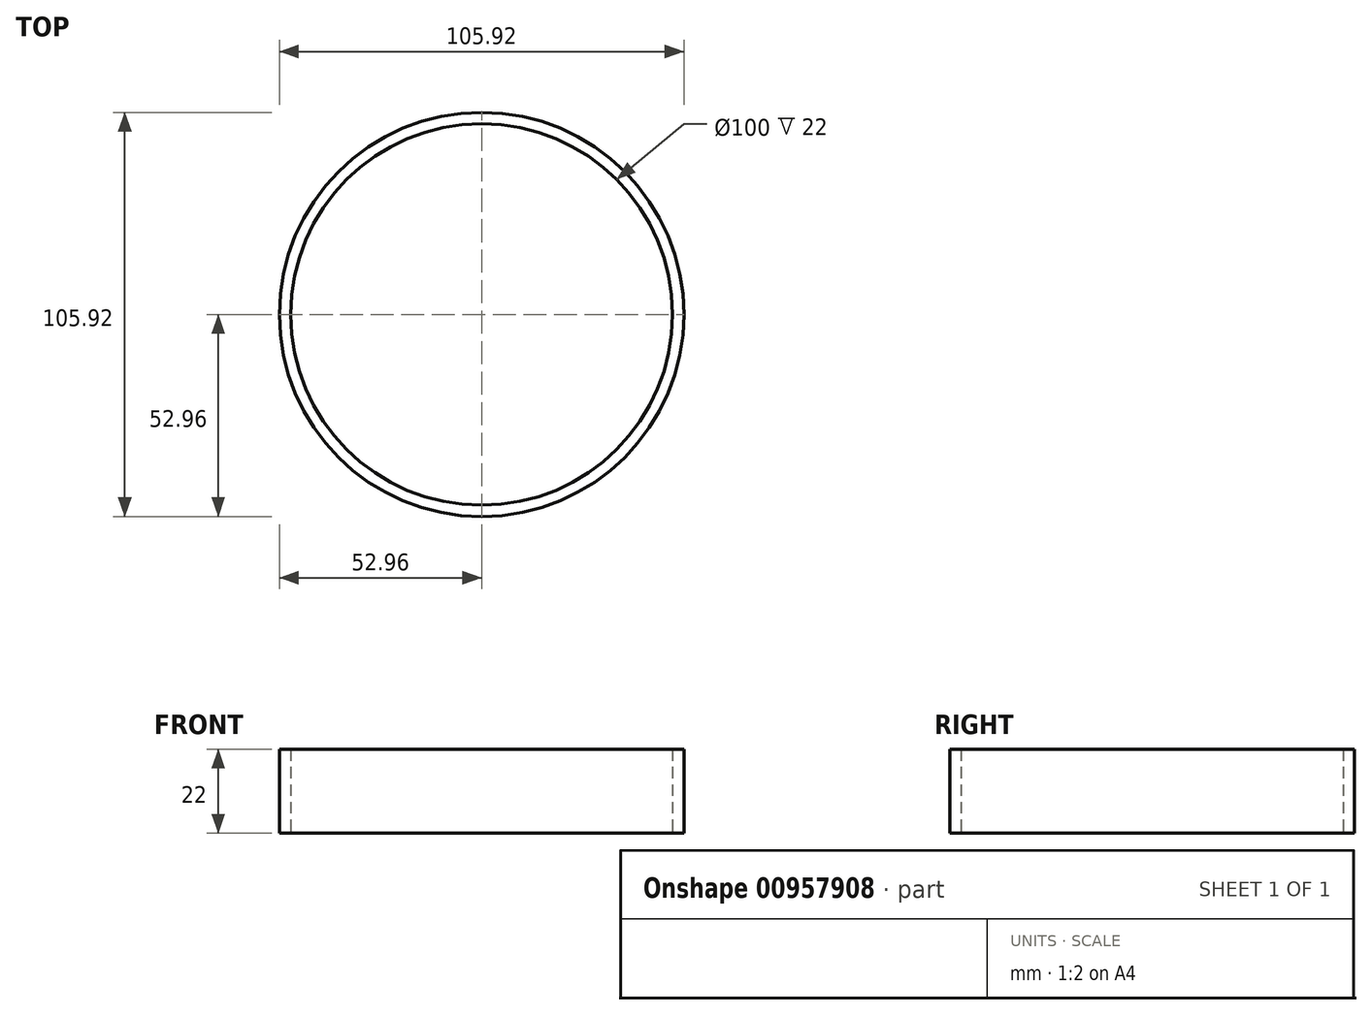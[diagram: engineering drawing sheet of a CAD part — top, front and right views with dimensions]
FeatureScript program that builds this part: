
annotation { "Feature Type Name" : "Feature", "Feature Type Description" : "" }
export const myFeature = defineFeature(function(context is Context, id is Id, definition is map)
    precondition{}
    {
        {
            var Q0;
            Q0=qCreatedBy(makeId("Top.planeOp"),FACE);
            var sketch = newSketch(context, id + "F0", { "sketchPlane" : qUnion([Q0])});
            skCircle(sketch, "E0", {"center": v(0, 0) * mm, "radius": 50 * mm});
            skCircle(sketch, "E1", {"center": v(0, 0) * mm, "radius": 52.96 * mm});
            skSolve(sketch);
        }
        {
            var Q0;
            Q0=makeQuery(id+"F0.imprint","IMPRINT",FACE,{"disambiguationData":[TD([[makeQuery(id+"F0.imprint","IMPRINT",EDGE,{"derivedFrom":sQuery(id+"F0.wireOp",EDGE,"E0")}),-1.0]])]});
            extrude(context, id + "F1", {"entities" : qUnion([Q0]), "depth" : 22 * mm, "offsetDistance" : 25 * mm});
        }
    });
